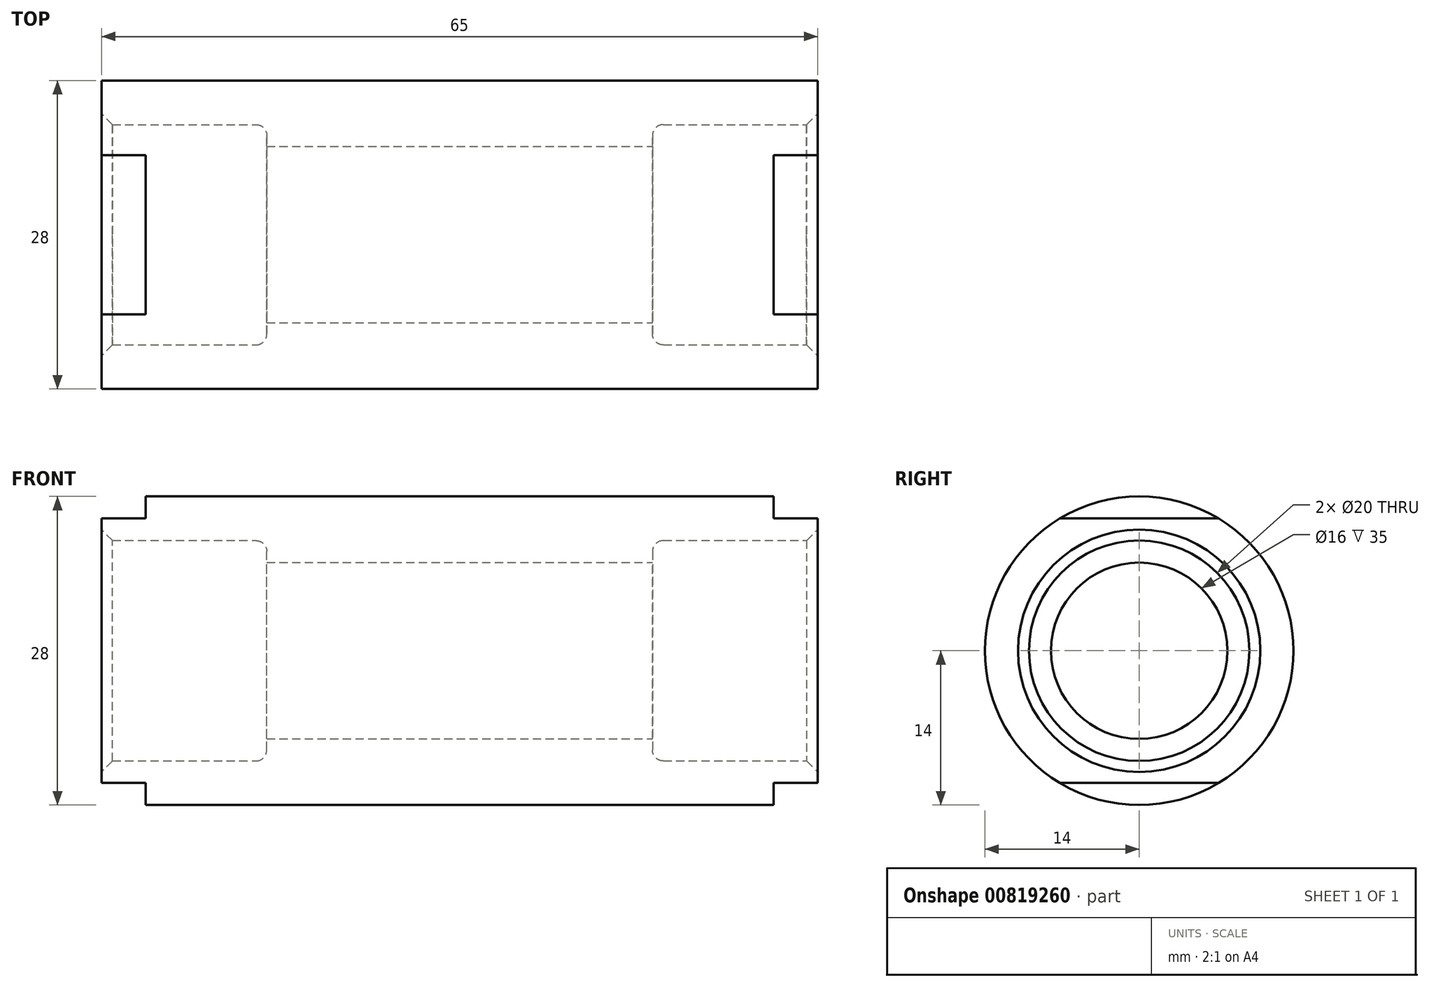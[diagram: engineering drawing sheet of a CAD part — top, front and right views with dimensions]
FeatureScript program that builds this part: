
annotation { "Feature Type Name" : "Feature", "Feature Type Description" : "" }
export const myFeature = defineFeature(function(context is Context, id is Id, definition is map)
    precondition{}
    {
        {
            var Q0;
            Q0=qCreatedBy(makeId("Front.planeOp"),FACE);
            var sketch = newSketch(context, id + "F0", { "sketchPlane" : qUnion([Q0])});
            skLineSegment(sketch, "E0", {"start": v(-32, 10) * mm, "end": v(-32, 14) * mm});
            skLineSegment(sketch, "E1", {"start": v(-32, 14) * mm, "end": v(33, 14) * mm});
            skLineSegment(sketch, "E2", {"start": v(33, 14) * mm, "end": v(33, 10) * mm});
            skLineSegment(sketch, "E3", {"start": v(33, 10) * mm, "end": v(18, 10) * mm});
            skLineSegment(sketch, "E4", {"start": v(18, 10) * mm, "end": v(18, 8) * mm});
            skLineSegment(sketch, "E5", {"start": v(18, 8) * mm, "end": v(-17, 8) * mm});
            skLineSegment(sketch, "E6", {"start": v(-17, 8) * mm, "end": v(-17, 10) * mm});
            skLineSegment(sketch, "E7", {"start": v(-17, 10) * mm, "end": v(-32, 10) * mm});
            skLineSegment(sketch, "E8", {"start": v(-32, 10) * mm, "end": v(-32, 10) * mm});
            skLineSegment(sketch, "E9", {"start": v(25.04, 0) * mm, "end": v(-16.3, 0) * mm, "construction": true});
            skSolve(sketch);
        }
        {
            var Q0;
            Q0=makeQuery(id+"F0.imprint","IMPRINT",FACE,{"disambiguationData":[TD([[makeQuery(id+"F0.imprint","IMPRINT",EDGE,{"derivedFrom":sQuery(id+"F0.wireOp",EDGE,"E0")}),-1.0]])]});
            var Q1;
            Q1 = qConstructionFilter(qBodyType(qCreatedBy(id + "F0" ,EDGE), BodyType.WIRE), ConstructionObject.NO);
            var Q2;
            Q2=sQuery(id+"F0.wireOp",EDGE,"E9");
            revolve(context, id + "F1", {"surfaceOperationType" : NewSurfaceOperationType.NEW, "entities" : qUnion([Q0]), "surfaceEntities" : qUnion([Q1]), "axis" : qUnion([Q2]), "revolveType" : RevolveType.FULL});
        }
        {
            var Q0;
            Q0=makeQuery(id+"F1.opRevolve","SWEPT_EDGE",EDGE,{"disambiguationData":[OSD([sQuery(id+"F0.wireOp",EDGE,"E3"),sQuery(id+"F0.wireOp",EDGE,"E4")])]});
            var Q1;
            Q1=makeQuery(id+"F1.opRevolve","SWEPT_EDGE",EDGE,{"disambiguationData":[OSD([sQuery(id+"F0.wireOp",EDGE,"E6"),sQuery(id+"F0.wireOp",EDGE,"E7")])]});
            fillet(context, id + "F2", {"entities" : qUnion([Q0, Q1]), "radius" : 1 * mm, "tangentPropagation" : true, "allowEdgeOverflow" : false});
        }
        {
            var Q0;
            Q0=makeQuery(id+"F1.opRevolve","SWEPT_EDGE",EDGE,{"disambiguationData":[OSD([sQuery(id+"F0.wireOp",EDGE,"E7"),sQuery(id+"F0.wireOp",EDGE,"E8")])]});
            var Q1;
            Q1=makeQuery(id+"F1.opRevolve","SWEPT_EDGE",EDGE,{"disambiguationData":[OSD([sQuery(id+"F0.wireOp",EDGE,"RhPujTbz-Bd1y-u0En-yAnw-qtvtZ00BfSfG"),sQuery(id+"F0.wireOp",EDGE,"E3")])]});
            chamfer(context, id + "F3", {"entities" : qUnion([Q0, Q1]), "width" : 1 * mm, "tangentPropagation" : true});
        }
        {
            var Q0;
            Q0=makeQuery(id+"F1.opRevolve","SWEPT_FACE",FACE,{"disambiguationData":[OSD([sQuery(id+"F0.wireOp",EDGE,"E0")])]});
            var sketch = newSketch(context, id + "F4", { "sketchPlane" : qUnion([Q0])});
            skLineSegment(sketch, "E10.bottom", {"start": v(-10, 14) * mm, "end": v(10, 14) * mm});
            skLineSegment(sketch, "E10.top", {"start": v(-10, 12) * mm, "end": v(10, 12) * mm});
            skLineSegment(sketch, "E10.left", {"start": v(-10, 14) * mm, "end": v(-10, 12) * mm});
            skLineSegment(sketch, "E10.right", {"start": v(10, 14) * mm, "end": v(10, 12) * mm});
            skLineSegment(sketch, "E11.MirrorCS", {"start": v(-10, -14) * mm, "end": v(10, -14) * mm});
            skLineSegment(sketch, "E12.MirrorCS", {"start": v(-10, -14) * mm, "end": v(-10, -12) * mm});
            skLineSegment(sketch, "E13.MirrorCS", {"start": v(-10, -12) * mm, "end": v(10, -12) * mm});
            skLineSegment(sketch, "E14.MirrorCS", {"start": v(10, -14) * mm, "end": v(10, -12) * mm});
            skSolve(sketch);
        }
        {
            var Q0;
            {var subQ1=sQuery(id+"F4.wireOp",EDGE,"E10.top");Q0=makeQuery(id+"F4.imprint","IMPRINT",FACE,{"disambiguationData":[TD([[makeQuery(id+"F4.imprint","IMPRINT",EDGE,{"derivedFrom":subQ1}),1.0]])]});}
            var Q1;
            {var subQ5=sQuery(id+"F4.wireOp",EDGE,"E13.MirrorCS");Q1=makeQuery(id+"F4.imprint","IMPRINT",FACE,{"disambiguationData":[TD([[makeQuery(id+"F4.imprint","IMPRINT",EDGE,{"derivedFrom":subQ5}),-1.0]])]});}
            extrude(context, id + "F5", {"entities" : qUnion([Q0, Q1]), "operationType" : NewBodyOperationType.REMOVE, "oppositeDirection" : true, "depth" : 4 * mm, "offsetDistance" : 25 * mm});
        }
        {
            var Q0;
            Q0=makeQuery(id+"F1.opRevolve","SWEPT_FACE",FACE,{"disambiguationData":[OSD([sQuery(id+"F0.wireOp",EDGE,"E2")])]});
            var sketch = newSketch(context, id + "F6", { "sketchPlane" : qUnion([Q0])});
            skLineSegment(sketch, "E15.bottom", {"start": v(-10, 14) * mm, "end": v(10, 14) * mm});
            skLineSegment(sketch, "E15.top", {"start": v(-10, 12) * mm, "end": v(10, 12) * mm});
            skLineSegment(sketch, "E15.left", {"start": v(-10, 14) * mm, "end": v(-10, 12) * mm});
            skLineSegment(sketch, "E15.right", {"start": v(10, 14) * mm, "end": v(10, 12) * mm});
            skLineSegment(sketch, "E16.MirrorCS", {"start": v(-10, -12) * mm, "end": v(10, -12) * mm});
            skLineSegment(sketch, "E17.MirrorCS", {"start": v(-10, -14) * mm, "end": v(-10, -12) * mm});
            skLineSegment(sketch, "E18.MirrorCS", {"start": v(-10, -14) * mm, "end": v(10, -14) * mm});
            skLineSegment(sketch, "E19.MirrorCS", {"start": v(10, -14) * mm, "end": v(10, -12) * mm});
            skSolve(sketch);
        }
        {
            var Q0;
            {var subQ0=sQuery(id+"F6.wireOp",EDGE,"E15.top");var subQ1=makeQuery(id+"F1.opRevolve","SWEPT_EDGE",EDGE,{"disambiguationData":[OSD([sQuery(id+"F0.wireOp",EDGE,"E1"),sQuery(id+"F0.wireOp",EDGE,"E2")])]});var subQ2=makeQuery(id+"F6.imprint","INTERSECT",VERTEX,{"disambiguationData":[OD(0.0)],"derivedFrom":[subQ1,subQ0]});Q0=makeQuery(id+"F6.imprint","IMPRINT",FACE,{"disambiguationData":[TD([[makeQuery(id+"F6.imprint","IMPRINT",EDGE,{"disambiguationData":[TD([[subQ2,-1.0]])],"derivedFrom":subQ0}),1.0]])]});}
            var Q1;
            {var subQ0=sQuery(id+"F6.wireOp",EDGE,"E16.MirrorCS");var subQ1=makeQuery(id+"F1.opRevolve","SWEPT_EDGE",EDGE,{"disambiguationData":[OSD([sQuery(id+"F0.wireOp",EDGE,"E1"),sQuery(id+"F0.wireOp",EDGE,"E2")])]});var subQ2=makeQuery(id+"F6.imprint","INTERSECT",VERTEX,{"disambiguationData":[OD(0.0)],"derivedFrom":[subQ1,subQ0]});Q1=makeQuery(id+"F6.imprint","IMPRINT",FACE,{"disambiguationData":[TD([[makeQuery(id+"F6.imprint","IMPRINT",EDGE,{"disambiguationData":[TD([[subQ2,-1.0]])],"derivedFrom":subQ0}),-1.0]])]});}
            extrude(context, id + "F7", {"entities" : qUnion([Q0, Q1]), "operationType" : NewBodyOperationType.REMOVE, "oppositeDirection" : true, "depth" : 4 * mm, "offsetDistance" : 25 * mm});
        }
    });
